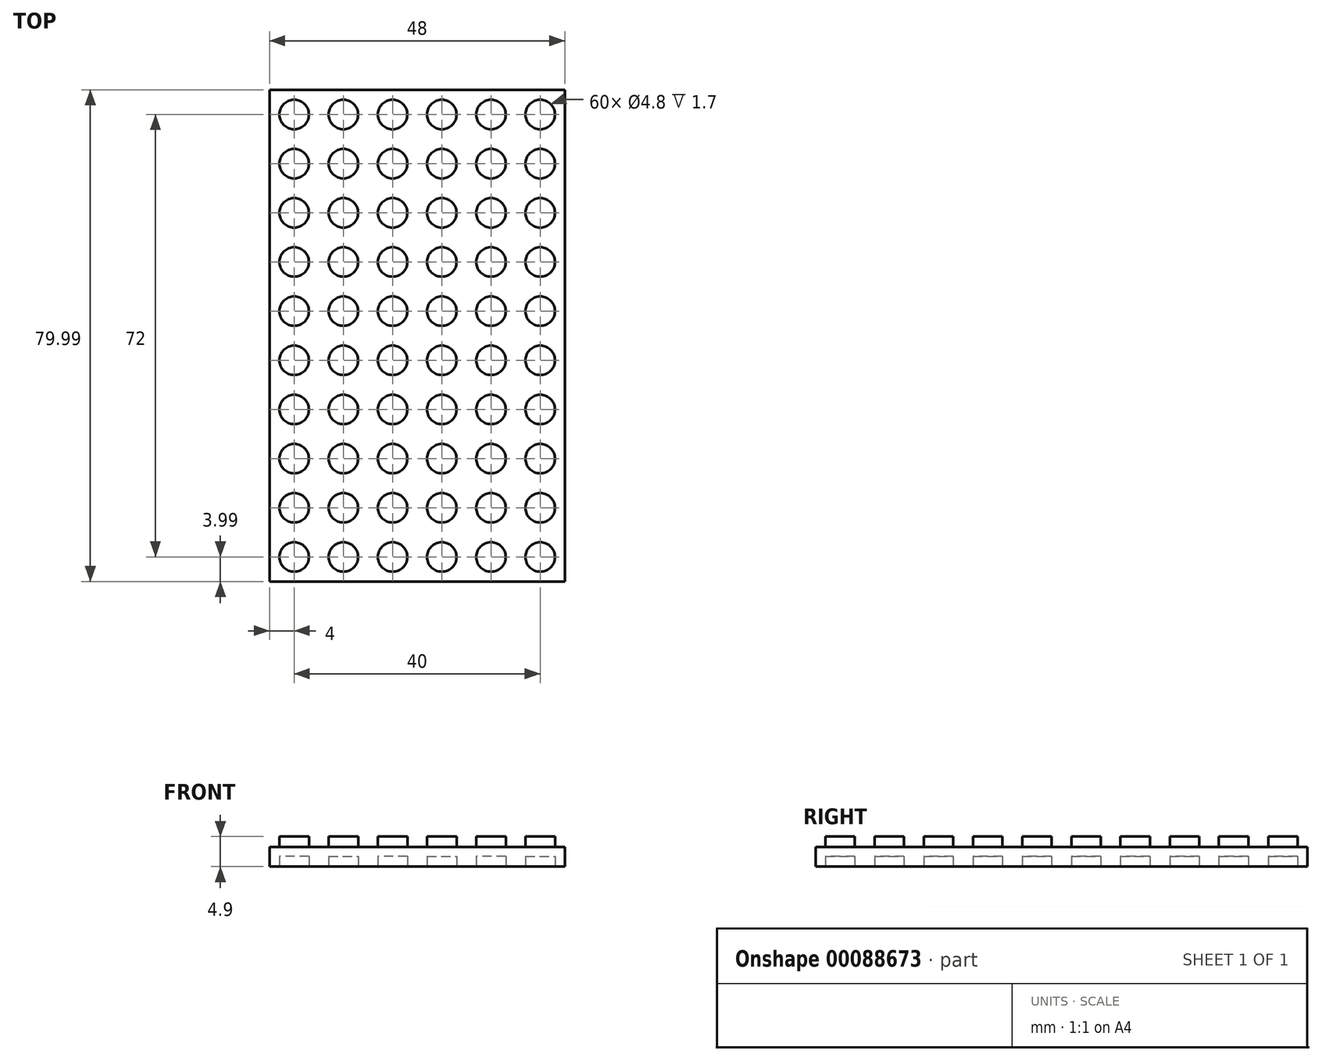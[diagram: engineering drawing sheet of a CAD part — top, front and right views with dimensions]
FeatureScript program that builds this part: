
annotation { "Feature Type Name" : "Feature", "Feature Type Description" : "" }
export const myFeature = defineFeature(function(context is Context, id is Id, definition is map)
    precondition{}
    {
        {
            var Q0;
            Q0=qCreatedBy(makeId("Front.planeOp"),FACE);
            var sketch = newSketch(context, id + "F0", { "sketchPlane" : qUnion([Q0])});
            skLineSegment(sketch, "E0.bottom", {"start": v(-4, 3.2) * mm, "end": v(-2.4, 3.2) * mm});
            skLineSegment(sketch, "E0.top", {"start": v(-4, 0) * mm, "end": v(4, 0) * mm});
            skLineSegment(sketch, "E0.left", {"start": v(-4, 3.2) * mm, "end": v(-4, 0) * mm});
            skLineSegment(sketch, "E0.right", {"start": v(4, 3.2) * mm, "end": v(4, 0) * mm});
            skLineSegment(sketch, "E1.top", {"start": v(-2.4, 4.9) * mm, "end": v(2.4, 4.9) * mm});
            skLineSegment(sketch, "E1.left", {"start": v(-2.4, 3.2) * mm, "end": v(-2.4, 4.9) * mm});
            skLineSegment(sketch, "E1.right", {"start": v(2.4, 3.2) * mm, "end": v(2.4, 4.9) * mm});
            skLineSegment(sketch, "E2", {"start": v(0, 0) * mm, "end": v(0, 24.04) * mm, "construction": true});
            skLineSegment(sketch, "E3.trimOffspring", {"start": v(2.4, 3.2) * mm, "end": v(4, 3.2) * mm});
            skSolve(sketch);
        }
        {
            var Q0;
            Q0=makeQuery(id+"F0.imprint","IMPRINT",FACE,{"disambiguationData":[TD([[makeQuery(id+"F0.imprint","IMPRINT",EDGE,{"derivedFrom":sQuery(id+"F0.wireOp",EDGE,"E0.bottom")}),-1.0]])]});
            extrude(context, id + "F1", {"entities" : qUnion([Q0]), "depth" : 8 * mm});
        }
        {
            var Q0;
            Q0=qCreatedBy(makeId("Top.planeOp"),FACE);
            var Q1;
            Q1=makeQuery(id+"F1.opExtrude","CAP_VERTEX",VERTEX,{"disambiguationData":[OSD([sQuery(id+"F0.wireOp",EDGE,"E1.top"),sQuery(id+"F0.wireOp",EDGE,"E1.right")])],"isStart":true});
            cPlane(context, id + "F2", {"entities" : qUnion([Q0, Q1]), "cplaneType" : CPlaneType.PLANE_POINT, "offset" : 152.4 * mm, "width" : 152.4 * mm, "height" : 152.4 * mm});
        }
        {
            var Q0;
            Q0=qCreatedBy(id+"F2.planeOp",FACE);
            var sketch = newSketch(context, id + "F3", { "sketchPlane" : qUnion([Q0])});
            skLineSegment(sketch, "E4.0", {"start": v(-4, -8) * mm, "end": v(-4, 0) * mm});
            skLineSegment(sketch, "E5.0", {"start": v(4, -8) * mm, "end": v(4, 0) * mm});
            skLineSegment(sketch, "E6", {"start": v(-4, 0) * mm, "end": v(4, 0) * mm});
            skLineSegment(sketch, "E7", {"start": v(-4, -8) * mm, "end": v(4, -8) * mm});
            skLineSegment(sketch, "E8", {"start": v(-4, 0) * mm, "end": v(4, -8) * mm, "construction": true});
            skLineSegment(sketch, "E9", {"start": v(-4, -8) * mm, "end": v(4, 0) * mm, "construction": true});
            skCircle(sketch, "E10", {"center": v(0, -4) * mm, "radius": 2.4 * mm});
            skSolve(sketch);
        }
        {
            var Q0;
            Q0=qSketchRegion(id+"F3",true);
            var Q1;
            Q1=makeQuery(id+"F1.opExtrude","SWEPT_FACE",FACE,{"disambiguationData":[OSD([sQuery(id+"F0.wireOp",EDGE,"E0.bottom")])]});
            extrude(context, id + "F4", {"entities" : qUnion([Q0]), "operationType" : NewBodyOperationType.REMOVE, "endBound" : BoundingType.UP_TO_SURFACE, "oppositeDirection" : true, "endBoundEntityFace" : qUnion([Q1]), "depth" : 25.4 * mm});
        }
        {
            var Q0;
            Q0=qCreatedBy(makeId("Top.planeOp"),FACE);
            var sketch = newSketch(context, id + "F5", { "sketchPlane" : qUnion([Q0])});
            skCircle(sketch, "E11.0", {"center": v(0, -4) * mm, "radius": 2.4 * mm});
            skSolve(sketch);
        }
        {
            var Q0;
            Q0=makeQuery(id+"F5.imprint","IMPRINT",FACE,{"disambiguationData":[TD([[makeQuery(id+"F5.imprint","IMPRINT",EDGE,{"derivedFrom":sQuery(id+"F5.wireOp",EDGE,"E11.0")}),1.0]])]});
            extrude(context, id + "F6", {"entities" : qUnion([Q0]), "operationType" : NewBodyOperationType.REMOVE, "depth" : 1.7 * mm});
        }
        {
            var Q0;
            Q0=qCreatedBy(makeId("Right.planeOp"),FACE);
            var Q1;
            Q1=makeQuery(id+"F1.opExtrude","CAP_VERTEX",VERTEX,{"disambiguationData":[OSD([sQuery(id+"F0.wireOp",EDGE,"E0.right"),sQuery(id+"F0.wireOp",EDGE,"E3.trimOffspring")])],"isStart":false});
            cPlane(context, id + "F7", {"entities" : qUnion([Q0, Q1]), "cplaneType" : CPlaneType.PLANE_POINT, "offset" : 152.4 * mm, "width" : 152.4 * mm, "height" : 152.4 * mm});
        }
        {
            var Q0;
            Q0=makeQuery(id+"F1.opExtrude","SWEPT_BODY",BODY,{"disambiguationData":[OSD([sQuery(id+"F0.wireOp",EDGE,"E0.bottom"),sQuery(id+"F0.wireOp",EDGE,"E0.top"),sQuery(id+"F0.wireOp",EDGE,"E0.left"),sQuery(id+"F0.wireOp",EDGE,"E0.right"),sQuery(id+"F0.wireOp",EDGE,"E1.top"),sQuery(id+"F0.wireOp",EDGE,"E1.left"),sQuery(id+"F0.wireOp",EDGE,"E1.right"),sQuery(id+"F0.wireOp",EDGE,"E3.trimOffspring")])]});
            var Q1;
            Q1=qCreatedBy(id+"F7.planeOp",FACE);
            mirror(context, id + "F8", {"operationType" : NewBodyOperationType.ADD, "entities" : qUnion([Q0]), "mirrorPlane" : qUnion([Q1])});
        }
        {
            var Q0;
            Q0=qCreatedBy(id+"F7.planeOp",FACE);
            var Q1;
            Q1=makeQuery(id+"F8.opPattern","COPY",VERTEX,{"derivedFrom":makeQuery(id+"F1.opExtrude","CAP_VERTEX",VERTEX,{"disambiguationData":[OSD([sQuery(id+"F0.wireOp",EDGE,"E0.bottom"),sQuery(id+"F0.wireOp",EDGE,"E0.left")])],"isStart":false}),"instanceName":"1"});
            cPlane(context, id + "F9", {"entities" : qUnion([Q0, Q1]), "cplaneType" : CPlaneType.PLANE_POINT, "offset" : 152.4 * mm, "width" : 152.4 * mm, "height" : 152.4 * mm});
        }
        {
            var Q0;
            Q0=makeQuery(id+"F1.opExtrude","SWEPT_BODY",BODY,{"disambiguationData":[OSD([sQuery(id+"F0.wireOp",EDGE,"E0.bottom"),sQuery(id+"F0.wireOp",EDGE,"E0.top"),sQuery(id+"F0.wireOp",EDGE,"E0.left"),sQuery(id+"F0.wireOp",EDGE,"E0.right"),sQuery(id+"F0.wireOp",EDGE,"E1.top"),sQuery(id+"F0.wireOp",EDGE,"E1.left"),sQuery(id+"F0.wireOp",EDGE,"E1.right"),sQuery(id+"F0.wireOp",EDGE,"E3.trimOffspring")])]});
            var Q1;
            Q1=qCreatedBy(id+"F9.planeOp",FACE);
            mirror(context, id + "F10", {"operationType" : NewBodyOperationType.ADD, "entities" : qUnion([Q0]), "mirrorPlane" : qUnion([Q1])});
        }
        {
            var Q0;
            Q0=qCreatedBy(makeId("Right.planeOp"),FACE);
            var Q1;
            Q1=makeQuery(id+"F10.opPattern","COPY",VERTEX,{"derivedFrom":makeQuery(id+"F1.opExtrude","CAP_VERTEX",VERTEX,{"disambiguationData":[OSD([sQuery(id+"F0.wireOp",EDGE,"E0.bottom"),sQuery(id+"F0.wireOp",EDGE,"E0.left")])],"isStart":false}),"instanceName":"1"});
            cPlane(context, id + "F11", {"entities" : qUnion([Q0, Q1]), "cplaneType" : CPlaneType.PLANE_POINT, "offset" : 152.4 * mm, "width" : 152.4 * mm, "height" : 152.4 * mm});
        }
        {
            var Q0;
            Q0=makeQuery(id+"F1.opExtrude","SWEPT_BODY",BODY,{"disambiguationData":[OSD([sQuery(id+"F0.wireOp",EDGE,"E0.bottom"),sQuery(id+"F0.wireOp",EDGE,"E0.top"),sQuery(id+"F0.wireOp",EDGE,"E0.left"),sQuery(id+"F0.wireOp",EDGE,"E0.right"),sQuery(id+"F0.wireOp",EDGE,"E1.top"),sQuery(id+"F0.wireOp",EDGE,"E1.left"),sQuery(id+"F0.wireOp",EDGE,"E1.right"),sQuery(id+"F0.wireOp",EDGE,"E3.trimOffspring")])]});
            var Q1;
            Q1=qCreatedBy(id+"F11.planeOp",FACE);
            mirror(context, id + "F12", {"operationType" : NewBodyOperationType.ADD, "entities" : qUnion([Q0]), "mirrorPlane" : qUnion([Q1])});
        }
        {
            var Q0;
            Q0=makeQuery(id+"F1.opExtrude","SWEPT_BODY",BODY,{"disambiguationData":[OSD([sQuery(id+"F0.wireOp",EDGE,"E0.bottom"),sQuery(id+"F0.wireOp",EDGE,"E0.top"),sQuery(id+"F0.wireOp",EDGE,"E0.left"),sQuery(id+"F0.wireOp",EDGE,"E0.right"),sQuery(id+"F0.wireOp",EDGE,"E1.top"),sQuery(id+"F0.wireOp",EDGE,"E1.left"),sQuery(id+"F0.wireOp",EDGE,"E1.right"),sQuery(id+"F0.wireOp",EDGE,"E3.trimOffspring")])]});
            var Q1;
            {var subQ0=makeQuery(id+"F1.opExtrude","CAP_FACE",FACE,{"disambiguationData":[OSD([sQuery(id+"F0.wireOp",EDGE,"E0.bottom"),sQuery(id+"F0.wireOp",EDGE,"E0.top"),sQuery(id+"F0.wireOp",EDGE,"E0.left"),sQuery(id+"F0.wireOp",EDGE,"E0.right"),sQuery(id+"F0.wireOp",EDGE,"E1.top"),sQuery(id+"F0.wireOp",EDGE,"E1.left"),sQuery(id+"F0.wireOp",EDGE,"E1.right"),sQuery(id+"F0.wireOp",EDGE,"E3.trimOffspring")])],"isStart":false});var subQ1=makeQuery(id+"F8.boolean.opBoolean","MERGE",FACE,{"derivedFrom":[subQ0,makeQuery(id+"F8.opPattern","COPY",FACE,{"derivedFrom":subQ0,"instanceName":"1"})]});var subQ2=makeQuery(id+"F10.boolean.opBoolean","MERGE",FACE,{"derivedFrom":[subQ1,makeQuery(id+"F10.opPattern","COPY",FACE,{"derivedFrom":subQ1,"instanceName":"1"})]});Q1=makeQuery(id+"F12.boolean.opBoolean","MERGE",FACE,{"derivedFrom":[subQ2,makeQuery(id+"F12.opPattern","COPY",FACE,{"derivedFrom":subQ2,"instanceName":"1"})]});}
            mirror(context, id + "F13", {"operationType" : NewBodyOperationType.ADD, "entities" : qUnion([Q0]), "mirrorPlane" : qUnion([Q1])});
        }
        {
            var Q0;
            Q0=makeQuery(id+"F1.opExtrude","SWEPT_BODY",BODY,{"disambiguationData":[OSD([sQuery(id+"F0.wireOp",EDGE,"E0.bottom"),sQuery(id+"F0.wireOp",EDGE,"E0.top"),sQuery(id+"F0.wireOp",EDGE,"E0.left"),sQuery(id+"F0.wireOp",EDGE,"E0.right"),sQuery(id+"F0.wireOp",EDGE,"E1.top"),sQuery(id+"F0.wireOp",EDGE,"E1.left"),sQuery(id+"F0.wireOp",EDGE,"E1.right"),sQuery(id+"F0.wireOp",EDGE,"E3.trimOffspring")])]});
            var Q1;
            {var subQ0=makeQuery(id+"F1.opExtrude","CAP_FACE",FACE,{"disambiguationData":[OSD([sQuery(id+"F0.wireOp",EDGE,"E0.bottom"),sQuery(id+"F0.wireOp",EDGE,"E0.top"),sQuery(id+"F0.wireOp",EDGE,"E0.left"),sQuery(id+"F0.wireOp",EDGE,"E0.right"),sQuery(id+"F0.wireOp",EDGE,"E1.top"),sQuery(id+"F0.wireOp",EDGE,"E1.left"),sQuery(id+"F0.wireOp",EDGE,"E1.right"),sQuery(id+"F0.wireOp",EDGE,"E3.trimOffspring")])],"isStart":true});var subQ1=makeQuery(id+"F8.boolean.opBoolean","MERGE",FACE,{"derivedFrom":[subQ0,makeQuery(id+"F8.opPattern","COPY",FACE,{"derivedFrom":subQ0,"instanceName":"1"})]});var subQ2=makeQuery(id+"F10.boolean.opBoolean","MERGE",FACE,{"derivedFrom":[subQ1,makeQuery(id+"F10.opPattern","COPY",FACE,{"derivedFrom":subQ1,"instanceName":"1"})]});Q1=makeQuery(id+"F13.opPattern","COPY",FACE,{"derivedFrom":makeQuery(id+"F12.boolean.opBoolean","MERGE",FACE,{"derivedFrom":[subQ2,makeQuery(id+"F12.opPattern","COPY",FACE,{"derivedFrom":subQ2,"instanceName":"1"})]}),"instanceName":"1"});}
            mirror(context, id + "F14", {"operationType" : NewBodyOperationType.ADD, "entities" : qUnion([Q0]), "mirrorPlane" : qUnion([Q1])});
        }
        {
            var Q0;
            Q0=makeQuery(id+"F1.opExtrude","SWEPT_BODY",BODY,{"disambiguationData":[OSD([sQuery(id+"F0.wireOp",EDGE,"E0.bottom"),sQuery(id+"F0.wireOp",EDGE,"E0.top"),sQuery(id+"F0.wireOp",EDGE,"E0.left"),sQuery(id+"F0.wireOp",EDGE,"E0.right"),sQuery(id+"F0.wireOp",EDGE,"E1.top"),sQuery(id+"F0.wireOp",EDGE,"E1.left"),sQuery(id+"F0.wireOp",EDGE,"E1.right"),sQuery(id+"F0.wireOp",EDGE,"E3.trimOffspring")])]});
            var Q1;
            {var subQ0=makeQuery(id+"F1.opExtrude","CAP_FACE",FACE,{"disambiguationData":[OSD([sQuery(id+"F0.wireOp",EDGE,"E0.bottom"),sQuery(id+"F0.wireOp",EDGE,"E0.top"),sQuery(id+"F0.wireOp",EDGE,"E0.left"),sQuery(id+"F0.wireOp",EDGE,"E0.right"),sQuery(id+"F0.wireOp",EDGE,"E1.top"),sQuery(id+"F0.wireOp",EDGE,"E1.left"),sQuery(id+"F0.wireOp",EDGE,"E1.right"),sQuery(id+"F0.wireOp",EDGE,"E3.trimOffspring")])],"isStart":true});var subQ1=makeQuery(id+"F8.boolean.opBoolean","MERGE",FACE,{"derivedFrom":[subQ0,makeQuery(id+"F8.opPattern","COPY",FACE,{"derivedFrom":subQ0,"instanceName":"1"})]});var subQ2=makeQuery(id+"F10.boolean.opBoolean","MERGE",FACE,{"derivedFrom":[subQ1,makeQuery(id+"F10.opPattern","COPY",FACE,{"derivedFrom":subQ1,"instanceName":"1"})]});Q1=makeQuery(id+"F14.opPattern","COPY",FACE,{"derivedFrom":makeQuery(id+"F12.boolean.opBoolean","MERGE",FACE,{"derivedFrom":[subQ2,makeQuery(id+"F12.opPattern","COPY",FACE,{"derivedFrom":subQ2,"instanceName":"1"})]}),"instanceName":"1"});}
            mirror(context, id + "F15", {"operationType" : NewBodyOperationType.ADD, "entities" : qUnion([Q0]), "mirrorPlane" : qUnion([Q1])});
        }
        {
            var Q0;
            Q0=makeQuery(id+"F1.opExtrude","SWEPT_BODY",BODY,{"disambiguationData":[OSD([sQuery(id+"F0.wireOp",EDGE,"E0.bottom"),sQuery(id+"F0.wireOp",EDGE,"E0.top"),sQuery(id+"F0.wireOp",EDGE,"E0.left"),sQuery(id+"F0.wireOp",EDGE,"E0.right"),sQuery(id+"F0.wireOp",EDGE,"E1.top"),sQuery(id+"F0.wireOp",EDGE,"E1.left"),sQuery(id+"F0.wireOp",EDGE,"E1.right"),sQuery(id+"F0.wireOp",EDGE,"E3.trimOffspring")])]});
            var Q1;
            {var subQ0=makeQuery(id+"F1.opExtrude","CAP_FACE",FACE,{"disambiguationData":[OSD([sQuery(id+"F0.wireOp",EDGE,"E0.bottom"),sQuery(id+"F0.wireOp",EDGE,"E0.top"),sQuery(id+"F0.wireOp",EDGE,"E0.left"),sQuery(id+"F0.wireOp",EDGE,"E0.right"),sQuery(id+"F0.wireOp",EDGE,"E1.top"),sQuery(id+"F0.wireOp",EDGE,"E1.left"),sQuery(id+"F0.wireOp",EDGE,"E1.right"),sQuery(id+"F0.wireOp",EDGE,"E3.trimOffspring")])],"isStart":true});var subQ1=makeQuery(id+"F8.boolean.opBoolean","MERGE",FACE,{"derivedFrom":[subQ0,makeQuery(id+"F8.opPattern","COPY",FACE,{"derivedFrom":subQ0,"instanceName":"1"})]});var subQ2=makeQuery(id+"F10.boolean.opBoolean","MERGE",FACE,{"derivedFrom":[subQ1,makeQuery(id+"F10.opPattern","COPY",FACE,{"derivedFrom":subQ1,"instanceName":"1"})]});Q1=makeQuery(id+"F15.opPattern","COPY",FACE,{"derivedFrom":makeQuery(id+"F12.boolean.opBoolean","MERGE",FACE,{"derivedFrom":[subQ2,makeQuery(id+"F12.opPattern","COPY",FACE,{"derivedFrom":subQ2,"instanceName":"1"})]}),"instanceName":"1"});}
            mirror(context, id + "F16", {"operationType" : NewBodyOperationType.ADD, "entities" : qUnion([Q0]), "mirrorPlane" : qUnion([Q1])});
        }
        {
            var Q0;
            {var subQ0=makeQuery(id+"F12.opPattern","COPY",FACE,{"derivedFrom":makeQuery(id+"F1.opExtrude","SWEPT_FACE",FACE,{"disambiguationData":[OSD([sQuery(id+"F0.wireOp",EDGE,"E0.left")])]}),"instanceName":"1"});var subQ1=makeQuery(id+"F13.boolean.opBoolean","MERGE",FACE,{"derivedFrom":[subQ0,makeQuery(id+"F13.opPattern","COPY",FACE,{"derivedFrom":subQ0,"instanceName":"1"})]});var subQ2=makeQuery(id+"F14.boolean.opBoolean","MERGE",FACE,{"derivedFrom":[subQ1,makeQuery(id+"F14.opPattern","COPY",FACE,{"derivedFrom":subQ1,"instanceName":"1"})]});var subQ3=makeQuery(id+"F15.boolean.opBoolean","MERGE",FACE,{"derivedFrom":[subQ2,makeQuery(id+"F15.opPattern","COPY",FACE,{"derivedFrom":subQ2,"instanceName":"1"})]});Q0=makeQuery(id+"F16.boolean.opBoolean","MERGE",FACE,{"derivedFrom":[subQ3,makeQuery(id+"F16.opPattern","COPY",FACE,{"derivedFrom":subQ3,"instanceName":"1"})]});}
            var sketch = newSketch(context, id + "F17", { "sketchPlane" : qUnion([Q0])});
            skLineSegment(sketch, "E12.bottom", {"start": v(20.87, 8.7) * mm, "end": v(-148.87, 8.7) * mm});
            skLineSegment(sketch, "E12.top", {"start": v(20.87, -8.7) * mm, "end": v(-148.87, -8.7) * mm});
            skLineSegment(sketch, "E12.left", {"start": v(20.87, 8.7) * mm, "end": v(20.87, -8.7) * mm});
            skLineSegment(sketch, "E12.right", {"start": v(-148.87, 8.7) * mm, "end": v(-148.87, -8.7) * mm});
            skPoint(sketch, "E12.middle", {"position": v(-64, 0) * mm});
            skSolve(sketch);
        }
        {
            var Q0;
            Q0 = qSketchRegion(id + "F17", true);
            extrude(context, id + "F18", {"entities" : qUnion([Q0]), "operationType" : NewBodyOperationType.REMOVE, "oppositeDirection" : true, "depth" : 16 * mm, "offsetDistance" : 25.4 * mm});
        }
        {
            var Q0;
            {var subQ0=makeQuery(id+"F1.opExtrude","CAP_FACE",FACE,{"disambiguationData":[OSD([sQuery(id+"F0.wireOp",EDGE,"E0.bottom"),sQuery(id+"F0.wireOp",EDGE,"E0.top"),sQuery(id+"F0.wireOp",EDGE,"E0.left"),sQuery(id+"F0.wireOp",EDGE,"E0.right"),sQuery(id+"F0.wireOp",EDGE,"E1.top"),sQuery(id+"F0.wireOp",EDGE,"E1.left"),sQuery(id+"F0.wireOp",EDGE,"E1.right"),sQuery(id+"F0.wireOp",EDGE,"E3.trimOffspring")])],"isStart":true});var subQ1=makeQuery(id+"F8.boolean.opBoolean","MERGE",FACE,{"derivedFrom":[subQ0,makeQuery(id+"F8.opPattern","COPY",FACE,{"derivedFrom":subQ0,"instanceName":"1"})]});var subQ2=makeQuery(id+"F10.boolean.opBoolean","MERGE",FACE,{"derivedFrom":[subQ1,makeQuery(id+"F10.opPattern","COPY",FACE,{"derivedFrom":subQ1,"instanceName":"1"})]});Q0=makeQuery(id+"F16.opPattern","COPY",FACE,{"derivedFrom":makeQuery(id+"F12.boolean.opBoolean","MERGE",FACE,{"derivedFrom":[subQ2,makeQuery(id+"F12.opPattern","COPY",FACE,{"derivedFrom":subQ2,"instanceName":"1"})]}),"instanceName":"1"});}
            var sketch = newSketch(context, id + "F19", { "sketchPlane" : qUnion([Q0])});
            skLineSegment(sketch, "E13.bottom", {"start": v(48.72, 21.08) * mm, "end": v(-8.72, 21.08) * mm});
            skLineSegment(sketch, "E13.top", {"start": v(48.72, -14.68) * mm, "end": v(-8.72, -14.68) * mm});
            skLineSegment(sketch, "E13.left", {"start": v(48.72, 21.08) * mm, "end": v(48.72, -14.68) * mm});
            skLineSegment(sketch, "E13.right", {"start": v(-8.72, 21.08) * mm, "end": v(-8.72, -14.68) * mm});
            skPoint(sketch, "E13.middle", {"position": v(20, 3.2) * mm});
            skSolve(sketch);
        }
        {
            var Q0;
            Q0 = qSketchRegion(id + "F19", true);
            extrude(context, id + "F20", {"entities" : qUnion([Q0]), "operationType" : NewBodyOperationType.REMOVE, "oppositeDirection" : true, "depth" : 0.63 * 76.2 * mm, "offsetDistance" : 25.4 * mm});
        }
    });
